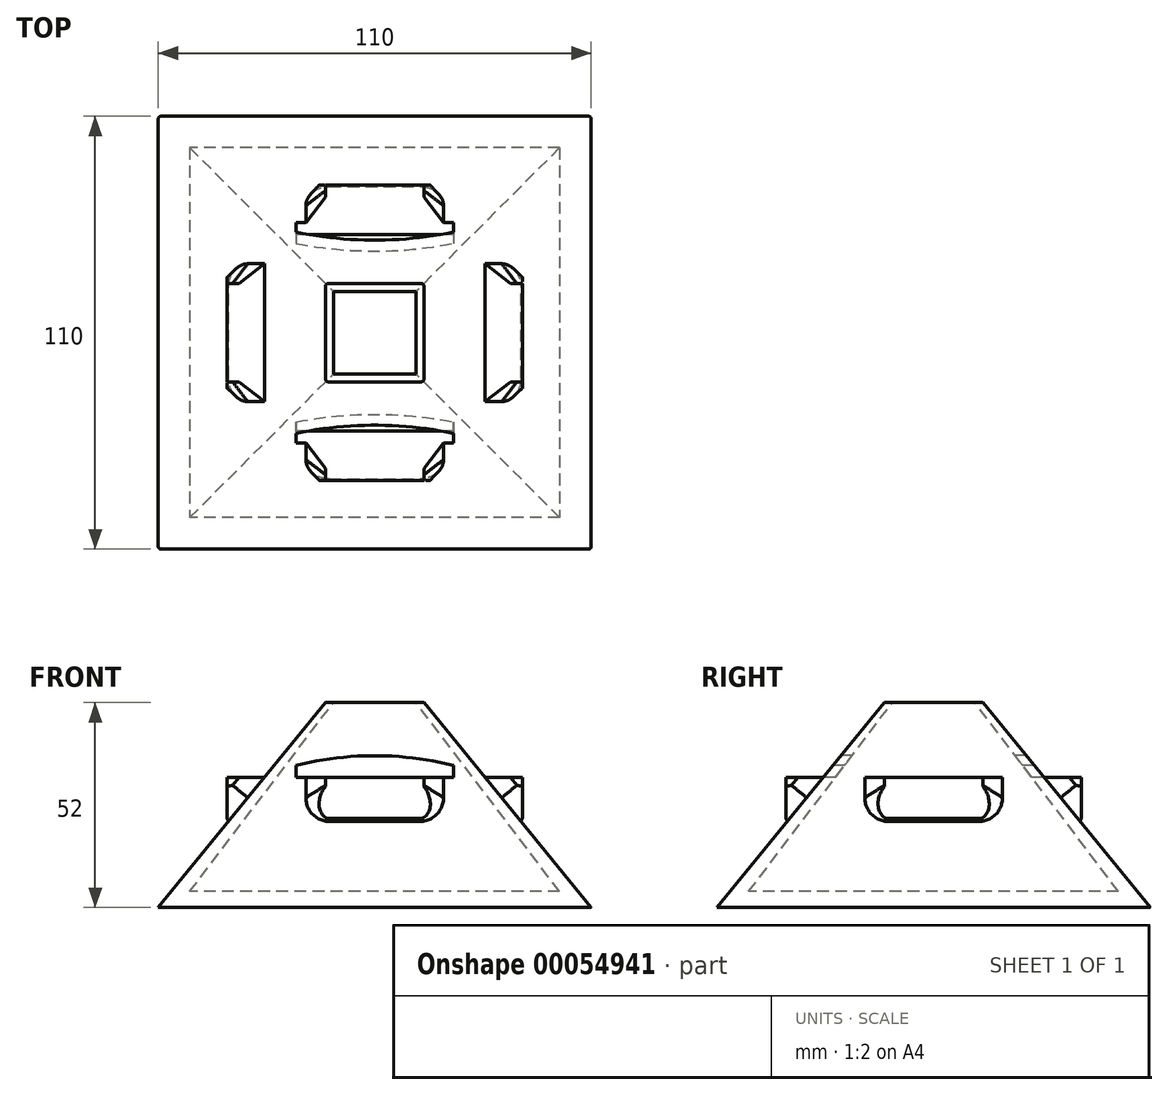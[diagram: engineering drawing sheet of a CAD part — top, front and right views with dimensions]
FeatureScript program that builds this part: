
annotation { "Feature Type Name" : "Feature", "Feature Type Description" : "" }
export const myFeature = defineFeature(function(context is Context, id is Id, definition is map)
    precondition{}
    {
        {
            var Q0;
            Q0=qCreatedBy(makeId("Top.planeOp"),FACE);
            var sketch = newSketch(context, id + "F0", { "sketchPlane" : qUnion([Q0])});
            skLineSegment(sketch, "E0.rect.bottom", {"start": v(55, 55) * mm, "end": v(-55, 55) * mm});
            skLineSegment(sketch, "E0.rect.top", {"start": v(55, -55) * mm, "end": v(-55, -55) * mm});
            skLineSegment(sketch, "E0.rect.left", {"start": v(55, 55) * mm, "end": v(55, -55) * mm});
            skLineSegment(sketch, "E0.rect.right", {"start": v(-55, 55) * mm, "end": v(-55, -55) * mm});
            skPoint(sketch, "E0.rect.middle", {"position": v(0, 0) * mm});
            skSolve(sketch);
        }
        {
            var Q0;
            Q0=qCreatedBy(makeId("Top.planeOp"),FACE);
            cPlane(context, id + "F1", {"entities" : qUnion([Q0]), "cplaneType" : CPlaneType.OFFSET, "offset" : 52 * mm, "width" : 150 * mm, "height" : 150 * mm});
        }
        {
            var Q0;
            Q0=qCreatedBy(id+"F1.planeOp",FACE);
            var sketch = newSketch(context, id + "F2", { "sketchPlane" : qUnion([Q0])});
            skLineSegment(sketch, "E1.rect.bottom", {"start": v(12.5, 12.5) * mm, "end": v(-12.5, 12.5) * mm});
            skLineSegment(sketch, "E1.rect.top", {"start": v(12.5, -12.5) * mm, "end": v(-12.5, -12.5) * mm});
            skLineSegment(sketch, "E1.rect.left", {"start": v(12.5, 12.5) * mm, "end": v(12.5, -12.5) * mm});
            skLineSegment(sketch, "E1.rect.right", {"start": v(-12.5, 12.5) * mm, "end": v(-12.5, -12.5) * mm});
            skPoint(sketch, "E1.rect.middle", {"position": v(0, 0) * mm});
            skSolve(sketch);
        }
        {
            var Q0;
            Q0=makeQuery(id+"F0.imprint","IMPRINT",FACE,{"disambiguationData":[TD([[makeQuery(id+"F0.imprint","IMPRINT",EDGE,{"derivedFrom":sQuery(id+"F0.wireOp",EDGE,"E0.rect.bottom")}),1.0]])]});
            var Q1;
            Q1=makeQuery(id+"F2.imprint","IMPRINT",FACE,{"disambiguationData":[TD([[makeQuery(id+"F2.imprint","IMPRINT",EDGE,{"derivedFrom":sQuery(id+"F2.wireOp",EDGE,"E1.rect.bottom")}),1.0]])]});
            loft(context, id + "F3", {"sheetProfilesArray" : [{ "sheetProfileEntities" : qUnion([Q0]) }, { "sheetProfileEntities" : qUnion([Q1]) }]});
        }
        {
            var Q0;
            Q0=qCreatedBy(makeId("Top.planeOp"),FACE);
            cPlane(context, id + "F4", {"entities" : qUnion([Q0]), "cplaneType" : CPlaneType.OFFSET, "offset" : 30 * mm, "width" : 150 * mm, "height" : 150 * mm});
        }
        {
            var Q0;
            Q0=qCreatedBy(id+"F4.planeOp",FACE);
            var sketch = newSketch(context, id + "F5", { "sketchPlane" : qUnion([Q0])});
            skLineSegment(sketch, "E2", {"start": v(-12.5, 37.5) * mm, "end": v(12.5, 37.5) * mm});
            skLineSegment(sketch, "E3", {"start": v(12.5, 37.5) * mm, "end": v(12.5, 12.5) * mm});
            skLineSegment(sketch, "E4", {"start": v(12.5, 12.5) * mm, "end": v(37.5, 12.5) * mm});
            skLineSegment(sketch, "E5", {"start": v(37.5, 12.5) * mm, "end": v(37.5, -12.5) * mm});
            skLineSegment(sketch, "E6", {"start": v(37.5, -12.5) * mm, "end": v(12.5, -12.5) * mm});
            skLineSegment(sketch, "E7", {"start": v(12.5, -12.5) * mm, "end": v(12.5, -37.5) * mm});
            skLineSegment(sketch, "E8", {"start": v(12.5, -37.5) * mm, "end": v(-12.5, -37.5) * mm});
            skLineSegment(sketch, "E9", {"start": v(-12.5, -37.5) * mm, "end": v(-12.5, -12.5) * mm});
            skLineSegment(sketch, "E10", {"start": v(-12.5, -12.5) * mm, "end": v(-37.5, -12.5) * mm});
            skLineSegment(sketch, "E11", {"start": v(-37.5, -12.5) * mm, "end": v(-37.5, 12.5) * mm});
            skLineSegment(sketch, "E12", {"start": v(-37.5, 12.5) * mm, "end": v(-12.5, 12.5) * mm});
            skLineSegment(sketch, "E13", {"start": v(-12.5, 12.5) * mm, "end": v(-12.5, 37.5) * mm});
            skSolve(sketch);
        }
        {
            var Q0;
            Q0=qSketchRegion(id+"F5",true);
            extrude(context, id + "F6", {"entities" : qUnion([Q0]), "operationType" : NewBodyOperationType.ADD, "depth" : 3 * mm});
        }
        {
            var Q0;
            Q0=qCreatedBy(makeId("Top.planeOp"),FACE);
            cPlane(context, id + "F7", {"entities" : qUnion([Q0]), "cplaneType" : CPlaneType.OFFSET, "offset" : 4 * mm, "width" : 150 * mm, "height" : 150 * mm});
        }
        {
            var Q0;
            Q0=qCreatedBy(id+"F7.planeOp",FACE);
            var sketch = newSketch(context, id + "F8", { "sketchPlane" : qUnion([Q0])});
            skLineSegment(sketch, "E14.rect.bottom", {"start": v(47, 47) * mm, "end": v(-47, 47) * mm});
            skLineSegment(sketch, "E14.rect.top", {"start": v(47, -47) * mm, "end": v(-47, -47) * mm});
            skLineSegment(sketch, "E14.rect.left", {"start": v(47, 47) * mm, "end": v(47, -47) * mm});
            skLineSegment(sketch, "E14.rect.right", {"start": v(-47, 47) * mm, "end": v(-47, -47) * mm});
            skPoint(sketch, "E14.rect.middle", {"position": v(0, 0) * mm});
            skSolve(sketch);
        }
        {
            var Q0;
            Q0=qCreatedBy(id+"F1.planeOp",FACE);
            var sketch = newSketch(context, id + "F9", { "sketchPlane" : qUnion([Q0])});
            skLineSegment(sketch, "E15.rect.bottom", {"start": v(10.5, 10.5) * mm, "end": v(-10.5, 10.5) * mm});
            skLineSegment(sketch, "E15.rect.top", {"start": v(10.5, -10.5) * mm, "end": v(-10.5, -10.5) * mm});
            skLineSegment(sketch, "E15.rect.left", {"start": v(10.5, 10.5) * mm, "end": v(10.5, -10.5) * mm});
            skLineSegment(sketch, "E15.rect.right", {"start": v(-10.5, 10.5) * mm, "end": v(-10.5, -10.5) * mm});
            skPoint(sketch, "E15.rect.middle", {"position": v(0, 0) * mm});
            skSolve(sketch);
        }
        {
            var Q1;
            Q1=qSketchRegion(id+"F8",true);
            var Q2;
            Q2=qSketchRegion(id+"F9",true);
            loft(context, id + "F10", {"operationType" : NewBodyOperationType.REMOVE, "sheetProfilesArray" : [{ "sheetProfileEntities" : qUnion([Q1]) }, { "sheetProfileEntities" : qUnion([Q2]) }]});
        }
        {
            var Q0;
            Q0=qCreatedBy(makeId("Front.planeOp"),FACE);
            var sketch = newSketch(context, id + "F11", { "sketchPlane" : qUnion([Q0])});
            skLineSegment(sketch, "E16.rect.top", {"start": v(-20, 33) * mm, "end": v(20, 33) * mm});
            skLineSegment(sketch, "E16.rect.left", {"start": v(-20, 36) * mm, "end": v(-20, 33) * mm});
            skLineSegment(sketch, "E16.rect.right", {"start": v(20, 36) * mm, "end": v(20, 33) * mm});
            skPoint(sketch, "E16.rect.middle", {"position": v(0, 34.5) * mm});
            skArc(sketch, "E17", {"start": v(20, 36) * mm, "mid": v(0, 38.54) * mm, "end": v(-20, 36) * mm});
            skSolve(sketch);
        }
        {
            var Q0;
            Q0=qSketchRegion(id+"F11",true);
            var Q1;
            Q1=makeQuery(id+"F3.opLoft","SWEPT_FACE",FACE,{"disambiguationData":[OSD([sQuery(id+"F0.wireOp",EDGE,"E0.rect.top"),sQuery(id+"F0.wireOp",EDGE,"E0.rect.left"),sQuery(id+"F0.wireOp",EDGE,"E0.rect.right"),sQuery(id+"F2.wireOp",EDGE,"E1.rect.top"),sQuery(id+"F2.wireOp",EDGE,"E1.rect.left"),sQuery(id+"F2.wireOp",EDGE,"E1.rect.right")])]});
            extrude(context, id + "F12", {"entities" : qUnion([Q0]), "operationType" : NewBodyOperationType.REMOVE, "endBound" : BoundingType.SYMMETRIC, "oppositeDirection" : true, "endBoundEntityFace" : qUnion([Q1]), "depth" : 75 * mm});
        }
        {
            var Q0;
            Q0=makeQuery(id+"F6.opExtrude","CAP_EDGE",EDGE,{"disambiguationData":[OSD([sQuery(id+"F5.wireOp",EDGE,"E13")])],"isStart":true});
            var Q1;
            Q1=makeQuery(id+"F3.opLoft","SWEPT_EDGE",EDGE,{"disambiguationData":[OSD([sQuery(id+"F0.wireOp",EDGE,"E0.rect.bottom"),sQuery(id+"F0.wireOp",EDGE,"E0.rect.right"),sQuery(id+"F2.wireOp",EDGE,"E1.rect.bottom"),sQuery(id+"F2.wireOp",EDGE,"E1.rect.right")])]});
            var Q2;
            Q2=makeQuery(id+"F6.opExtrude","CAP_EDGE",EDGE,{"disambiguationData":[OSD([sQuery(id+"F5.wireOp",EDGE,"E12")])],"isStart":true});
            var Q3;
            Q3=makeQuery(id+"F6.opExtrude","CAP_EDGE",EDGE,{"disambiguationData":[OSD([sQuery(id+"F5.wireOp",EDGE,"E3")])],"isStart":true});
            var Q4;
            Q4=makeQuery(id+"F3.opLoft","SWEPT_EDGE",EDGE,{"disambiguationData":[OSD([sQuery(id+"F0.wireOp",EDGE,"E0.rect.bottom"),sQuery(id+"F0.wireOp",EDGE,"E0.rect.left"),sQuery(id+"F2.wireOp",EDGE,"E1.rect.bottom"),sQuery(id+"F2.wireOp",EDGE,"E1.rect.left")])]});
            var Q5;
            Q5=makeQuery(id+"F6.opExtrude","CAP_EDGE",EDGE,{"disambiguationData":[OSD([sQuery(id+"F5.wireOp",EDGE,"E4")])],"isStart":true});
            var Q6;
            Q6=makeQuery(id+"F6.opExtrude","CAP_EDGE",EDGE,{"disambiguationData":[OSD([sQuery(id+"F5.wireOp",EDGE,"E6")])],"isStart":true});
            var Q7;
            Q7=makeQuery(id+"F3.opLoft","SWEPT_EDGE",EDGE,{"disambiguationData":[OSD([sQuery(id+"F0.wireOp",EDGE,"E0.rect.top"),sQuery(id+"F0.wireOp",EDGE,"E0.rect.left"),sQuery(id+"F2.wireOp",EDGE,"E1.rect.top"),sQuery(id+"F2.wireOp",EDGE,"E1.rect.left")])]});
            var Q8;
            Q8=makeQuery(id+"F6.opExtrude","CAP_EDGE",EDGE,{"disambiguationData":[OSD([sQuery(id+"F5.wireOp",EDGE,"E7")])],"isStart":true});
            var Q9;
            Q9=makeQuery(id+"F6.opExtrude","CAP_EDGE",EDGE,{"disambiguationData":[OSD([sQuery(id+"F5.wireOp",EDGE,"E9")])],"isStart":true});
            var Q10;
            Q10=makeQuery(id+"F3.opLoft","SWEPT_EDGE",EDGE,{"disambiguationData":[OSD([sQuery(id+"F0.wireOp",EDGE,"E0.rect.top"),sQuery(id+"F0.wireOp",EDGE,"E0.rect.right"),sQuery(id+"F2.wireOp",EDGE,"E1.rect.top"),sQuery(id+"F2.wireOp",EDGE,"E1.rect.right")])]});
            var Q11;
            Q11=makeQuery(id+"F6.opExtrude","CAP_EDGE",EDGE,{"disambiguationData":[OSD([sQuery(id+"F5.wireOp",EDGE,"E10")])],"isStart":true});
            fillet(context, id + "F13", {"entities" : qUnion([Q0, Q1, Q2, Q3, Q4, Q5, Q6, Q7, Q8, Q9, Q10, Q11]), "radius" : 1 * mm, "tangentPropagation" : true, "allowEdgeOverflow" : false});
        }
        {
            var Q0;
            Q0=makeQuery(id+"F6.boolean.opBoolean","INTERSECT",EDGE,{"derivedFrom":[makeQuery(id+"F3.opLoft","SWEPT_FACE",FACE,{"disambiguationData":[OSD([sQuery(id+"F0.wireOp",EDGE,"E0.rect.top"),sQuery(id+"F0.wireOp",EDGE,"E0.rect.left"),sQuery(id+"F0.wireOp",EDGE,"E0.rect.right"),sQuery(id+"F2.wireOp",EDGE,"E1.rect.top"),sQuery(id+"F2.wireOp",EDGE,"E1.rect.left"),sQuery(id+"F2.wireOp",EDGE,"E1.rect.right")])]}),makeQuery(id+"F6.opExtrude","CAP_FACE",FACE,{"disambiguationData":[OSD([sQuery(id+"F5.wireOp",EDGE,"E2"),sQuery(id+"F5.wireOp",EDGE,"E3"),sQuery(id+"F5.wireOp",EDGE,"E4"),sQuery(id+"F5.wireOp",EDGE,"E5"),sQuery(id+"F5.wireOp",EDGE,"E6"),sQuery(id+"F5.wireOp",EDGE,"E7"),sQuery(id+"F5.wireOp",EDGE,"E8"),sQuery(id+"F5.wireOp",EDGE,"E9"),sQuery(id+"F5.wireOp",EDGE,"E10"),sQuery(id+"F5.wireOp",EDGE,"E11"),sQuery(id+"F5.wireOp",EDGE,"E12"),sQuery(id+"F5.wireOp",EDGE,"E13")])],"isStart":true})]});
            var Q1;
            Q1=makeQuery(id+"F6.boolean.opBoolean","INTERSECT",EDGE,{"derivedFrom":[makeQuery(id+"F3.opLoft","SWEPT_FACE",FACE,{"disambiguationData":[OSD([sQuery(id+"F0.wireOp",EDGE,"E0.rect.bottom"),sQuery(id+"F0.wireOp",EDGE,"E0.rect.top"),sQuery(id+"F0.wireOp",EDGE,"E0.rect.left"),sQuery(id+"F2.wireOp",EDGE,"E1.rect.bottom"),sQuery(id+"F2.wireOp",EDGE,"E1.rect.top"),sQuery(id+"F2.wireOp",EDGE,"E1.rect.left")])]}),makeQuery(id+"F6.opExtrude","CAP_FACE",FACE,{"disambiguationData":[OSD([sQuery(id+"F5.wireOp",EDGE,"E2"),sQuery(id+"F5.wireOp",EDGE,"E3"),sQuery(id+"F5.wireOp",EDGE,"E4"),sQuery(id+"F5.wireOp",EDGE,"E5"),sQuery(id+"F5.wireOp",EDGE,"E6"),sQuery(id+"F5.wireOp",EDGE,"E7"),sQuery(id+"F5.wireOp",EDGE,"E8"),sQuery(id+"F5.wireOp",EDGE,"E9"),sQuery(id+"F5.wireOp",EDGE,"E10"),sQuery(id+"F5.wireOp",EDGE,"E11"),sQuery(id+"F5.wireOp",EDGE,"E12"),sQuery(id+"F5.wireOp",EDGE,"E13")])],"isStart":true})]});
            var Q2;
            Q2=makeQuery(id+"F6.boolean.opBoolean","INTERSECT",EDGE,{"derivedFrom":[makeQuery(id+"F3.opLoft","SWEPT_FACE",FACE,{"disambiguationData":[OSD([sQuery(id+"F0.wireOp",EDGE,"E0.rect.bottom"),sQuery(id+"F0.wireOp",EDGE,"E0.rect.left"),sQuery(id+"F0.wireOp",EDGE,"E0.rect.right"),sQuery(id+"F2.wireOp",EDGE,"E1.rect.bottom"),sQuery(id+"F2.wireOp",EDGE,"E1.rect.left"),sQuery(id+"F2.wireOp",EDGE,"E1.rect.right")])]}),makeQuery(id+"F6.opExtrude","CAP_FACE",FACE,{"disambiguationData":[OSD([sQuery(id+"F5.wireOp",EDGE,"E2"),sQuery(id+"F5.wireOp",EDGE,"E3"),sQuery(id+"F5.wireOp",EDGE,"E4"),sQuery(id+"F5.wireOp",EDGE,"E5"),sQuery(id+"F5.wireOp",EDGE,"E6"),sQuery(id+"F5.wireOp",EDGE,"E7"),sQuery(id+"F5.wireOp",EDGE,"E8"),sQuery(id+"F5.wireOp",EDGE,"E9"),sQuery(id+"F5.wireOp",EDGE,"E10"),sQuery(id+"F5.wireOp",EDGE,"E11"),sQuery(id+"F5.wireOp",EDGE,"E12"),sQuery(id+"F5.wireOp",EDGE,"E13")])],"isStart":true})]});
            var Q3;
            Q3=makeQuery(id+"F6.boolean.opBoolean","INTERSECT",EDGE,{"derivedFrom":[makeQuery(id+"F3.opLoft","SWEPT_FACE",FACE,{"disambiguationData":[OSD([sQuery(id+"F0.wireOp",EDGE,"E0.rect.bottom"),sQuery(id+"F0.wireOp",EDGE,"E0.rect.top"),sQuery(id+"F0.wireOp",EDGE,"E0.rect.right"),sQuery(id+"F2.wireOp",EDGE,"E1.rect.bottom"),sQuery(id+"F2.wireOp",EDGE,"E1.rect.top"),sQuery(id+"F2.wireOp",EDGE,"E1.rect.right")])]}),makeQuery(id+"F6.opExtrude","CAP_FACE",FACE,{"disambiguationData":[OSD([sQuery(id+"F5.wireOp",EDGE,"E2"),sQuery(id+"F5.wireOp",EDGE,"E3"),sQuery(id+"F5.wireOp",EDGE,"E4"),sQuery(id+"F5.wireOp",EDGE,"E5"),sQuery(id+"F5.wireOp",EDGE,"E6"),sQuery(id+"F5.wireOp",EDGE,"E7"),sQuery(id+"F5.wireOp",EDGE,"E8"),sQuery(id+"F5.wireOp",EDGE,"E9"),sQuery(id+"F5.wireOp",EDGE,"E10"),sQuery(id+"F5.wireOp",EDGE,"E11"),sQuery(id+"F5.wireOp",EDGE,"E12"),sQuery(id+"F5.wireOp",EDGE,"E13")])],"isStart":true})]});
            chamfer(context, id + "F14", {"entities" : qUnion([Q0, Q1, Q2, Q3]), "width" : 5 * mm, "tangentPropagation" : true});
        }
    });
